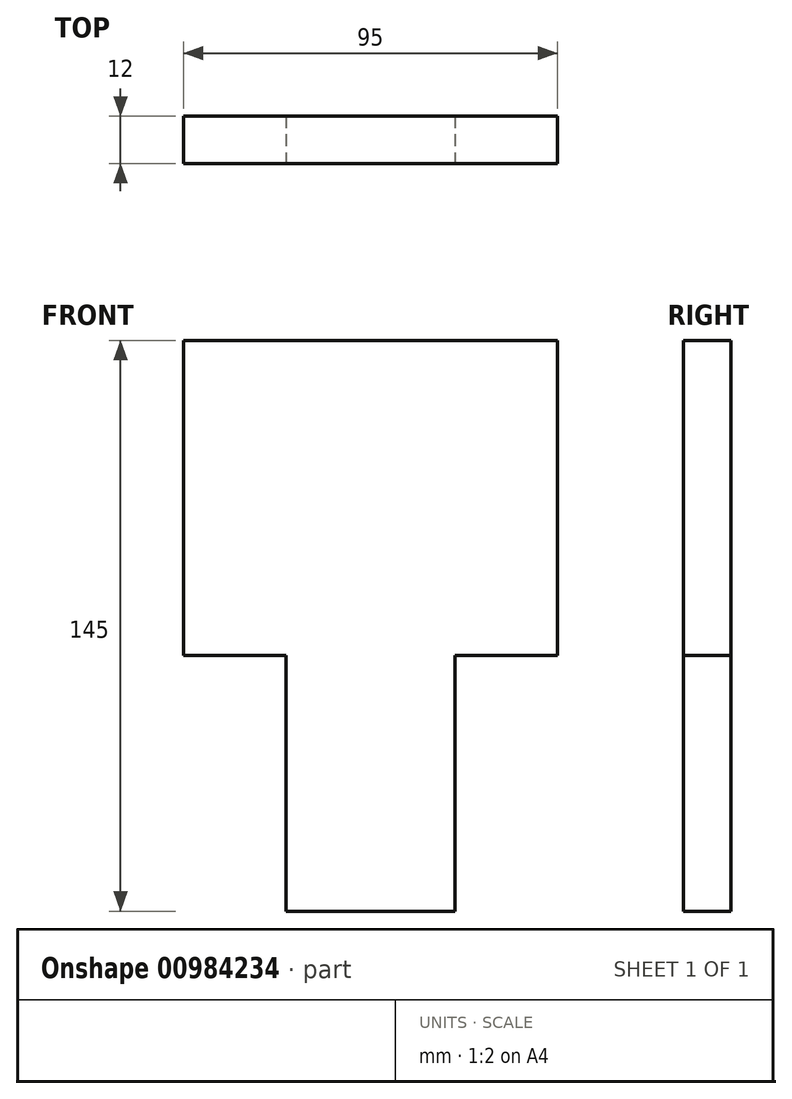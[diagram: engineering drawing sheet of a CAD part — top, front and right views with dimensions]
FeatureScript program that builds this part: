
annotation { "Feature Type Name" : "Feature", "Feature Type Description" : "" }
export const myFeature = defineFeature(function(context is Context, id is Id, definition is map)
    precondition{}
    {
        {
            var Q0;
            Q0=qCreatedBy(makeId("Front.planeOp"),FACE);
            var sketch = newSketch(context, id + "F0", { "sketchPlane" : qUnion([Q0])});
            skLineSegment(sketch, "E0.bottom", {"start": v(47.5, 72.5) * mm, "end": v(-47.5, 72.5) * mm});
            skLineSegment(sketch, "E0.top", {"start": v(47.5, -72.5) * mm, "end": v(-47.5, -72.5) * mm});
            skLineSegment(sketch, "E0.left", {"start": v(47.5, 72.5) * mm, "end": v(47.5, -72.5) * mm});
            skLineSegment(sketch, "E0.right", {"start": v(-47.5, 72.5) * mm, "end": v(-47.5, -72.5) * mm});
            skPoint(sketch, "E0.middle", {"position": v(0, 0) * mm});
            skSolve(sketch);
        }
        {
            var Q0;
            Q0=makeQuery(id+"F0.imprint","IMPRINT",FACE,{"disambiguationData":[TD([[makeQuery(id+"F0.imprint","IMPRINT",EDGE,{"derivedFrom":sQuery(id+"F0.wireOp",EDGE,"E0.bottom")}),1.0]])]});
            extrude(context, id + "F1", {"entities" : qUnion([Q0]), "oppositeDirection" : true, "depth" : 12 * mm, "offsetDistance" : 25 * mm});
        }
        {
            var Q0;
            Q0=makeQuery(id+"F1.opExtrude","CAP_FACE",FACE,{"disambiguationData":[OSD([sQuery(id+"F0.wireOp",EDGE,"E0.bottom"),sQuery(id+"F0.wireOp",EDGE,"E0.top"),sQuery(id+"F0.wireOp",EDGE,"E0.left"),sQuery(id+"F0.wireOp",EDGE,"E0.right")])],"isStart":true});
            var sketch = newSketch(context, id + "F2", { "sketchPlane" : qUnion([Q0])});
            skLineSegment(sketch, "E1.bottom", {"start": v(47.5, -72.5) * mm, "end": v(21.5, -72.5) * mm});
            skLineSegment(sketch, "E1.top", {"start": v(47.5, -7.5) * mm, "end": v(21.5, -7.5) * mm});
            skLineSegment(sketch, "E1.left", {"start": v(47.5, -72.5) * mm, "end": v(47.5, -7.5) * mm});
            skLineSegment(sketch, "E1.right", {"start": v(21.5, -72.5) * mm, "end": v(21.5, -7.5) * mm});
            skSolve(sketch);
        }
        {
            var Q0;
            Q0=makeQuery(id+"F2.imprint","IMPRINT",FACE,{"disambiguationData":[TD([[makeQuery(id+"F2.imprint","IMPRINT",EDGE,{"derivedFrom":sQuery(id+"F2.wireOp",EDGE,"E1.bottom")}),-1.0]])]});
            extrude(context, id + "F3", {"entities" : qUnion([Q0]), "operationType" : NewBodyOperationType.REMOVE, "oppositeDirection" : true, "depth" : 15 * mm, "offsetDistance" : 25 * mm});
        }
        {
            var Q0;
            Q0=makeQuery(id+"F1.opExtrude","CAP_FACE",FACE,{"disambiguationData":[OSD([sQuery(id+"F0.wireOp",EDGE,"E0.bottom"),sQuery(id+"F0.wireOp",EDGE,"E0.top"),sQuery(id+"F0.wireOp",EDGE,"E0.left"),sQuery(id+"F0.wireOp",EDGE,"E0.right")])],"isStart":true});
            var sketch = newSketch(context, id + "F4", { "sketchPlane" : qUnion([Q0])});
            skLineSegment(sketch, "E2.bottom", {"start": v(-47.5, -72.5) * mm, "end": v(-21.5, -72.5) * mm});
            skLineSegment(sketch, "E2.top", {"start": v(-47.5, -7.5) * mm, "end": v(-21.5, -7.5) * mm});
            skLineSegment(sketch, "E2.left", {"start": v(-47.5, -72.5) * mm, "end": v(-47.5, -7.5) * mm});
            skLineSegment(sketch, "E2.right", {"start": v(-21.5, -72.5) * mm, "end": v(-21.5, -7.5) * mm});
            skSolve(sketch);
        }
        {
            var Q0;
            Q0=makeQuery(id+"F4.imprint","IMPRINT",FACE,{"disambiguationData":[TD([[makeQuery(id+"F4.imprint","IMPRINT",EDGE,{"derivedFrom":sQuery(id+"F4.wireOp",EDGE,"E2.bottom")}),-1.0]])]});
            extrude(context, id + "F5", {"entities" : qUnion([Q0]), "operationType" : NewBodyOperationType.REMOVE, "oppositeDirection" : true, "depth" : 15 * mm, "offsetDistance" : 25 * mm});
        }
    });
